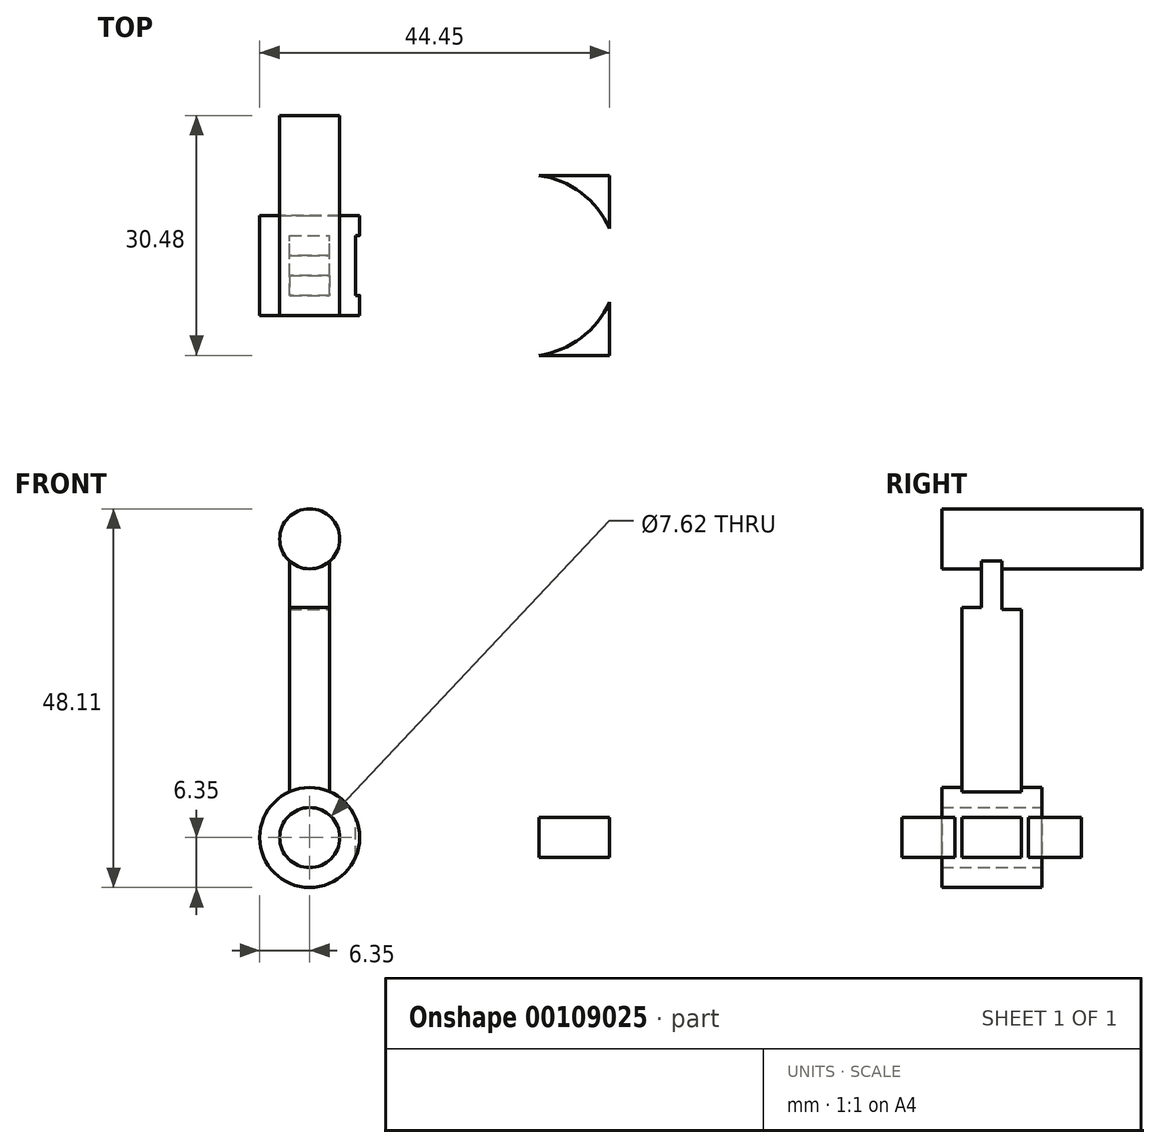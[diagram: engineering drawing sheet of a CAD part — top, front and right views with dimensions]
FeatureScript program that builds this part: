
annotation { "Feature Type Name" : "Feature", "Feature Type Description" : "" }
export const myFeature = defineFeature(function(context is Context, id is Id, definition is map)
    precondition{}
    {
        {
            var Q0;
            Q0=qCreatedBy(makeId("Front.planeOp"),FACE);
            var sketch = newSketch(context, id + "F0", { "sketchPlane" : qUnion([Q0])});
            skCircle(sketch, "E0", {"center": v(0, 0) * mm, "radius": 3.81 * mm});
            skCircle(sketch, "E1", {"center": v(0, 0) * mm, "radius": 6.35 * mm});
            skSolve(sketch);
        }
        {
            var Q0;
            Q0=makeQuery(id+"F0.imprint","IMPRINT",FACE,{"disambiguationData":[TD([[makeQuery(id+"F0.imprint","IMPRINT",EDGE,{"derivedFrom":sQuery(id+"F0.wireOp",EDGE,"E0")}),-1.0]])]});
            extrude(context, id + "F1", {"entities" : qUnion([Q0]), "depth" : 12.7 * mm});
        }
        {
            var Q0;
            Q0=qCreatedBy(makeId("Top.planeOp"),FACE);
            var sketch = newSketch(context, id + "F2", { "sketchPlane" : qUnion([Q0])});
            skLineSegment(sketch, "E2", {"start": v(0, 0) * mm, "end": v(-6.35, 0) * mm});
            skLineSegment(sketch, "E3", {"start": v(-6.35, -6.35) * mm, "end": v(-6.35, -10.16) * mm});
            skLineSegment(sketch, "E4", {"start": v(-6.35, -6.35) * mm, "end": v(-6.35, -2.54) * mm});
            skSolve(sketch);
        }
        {
            var Q0;
            Q0=qCreatedBy(makeId("Right.planeOp"),FACE);
            var sketch = newSketch(context, id + "F3", { "sketchPlane" : qUnion([Q0])});
            skLineSegment(sketch, "E5", {"start": v(-2.54, 0) * mm, "end": v(-2.54, 2.54) * mm});
            skLineSegment(sketch, "E6", {"start": v(-2.54, 0) * mm, "end": v(-2.54, -2.54) * mm});
            skLineSegment(sketch, "E7", {"start": v(-2.54, -2.54) * mm, "end": v(-10.16, -2.54) * mm});
            skLineSegment(sketch, "E8", {"start": v(-10.16, -2.54) * mm, "end": v(-10.16, 0) * mm});
            skLineSegment(sketch, "E9", {"start": v(-10.16, 0) * mm, "end": v(-10.16, 2.54) * mm});
            skLineSegment(sketch, "E10", {"start": v(-10.16, 2.54) * mm, "end": v(-2.54, 2.54) * mm});
            skSolve(sketch);
        }
        {
            var Q0;
            Q0=makeQuery(id+"F3.imprint","IMPRINT",FACE,{"disambiguationData":[TD([[makeQuery(id+"F3.imprint","IMPRINT",EDGE,{"derivedFrom":sQuery(id+"F3.wireOp",EDGE,"E5")}),1.0]])]});
            extrude(context, id + "F4", {"entities" : qUnion([Q0]), "operationType" : NewBodyOperationType.ADD, "depth" : 38.1 * mm});
        }
        {
            var Q0;
            Q0=makeQuery(id+"F0.imprint","IMPRINT",FACE,{"disambiguationData":[TD([[makeQuery(id+"F0.imprint","IMPRINT",EDGE,{"derivedFrom":sQuery(id+"F0.wireOp",EDGE,"E0")}),1.0]])]});
            extrude(context, id + "F5", {"entities" : qUnion([Q0]), "operationType" : NewBodyOperationType.REMOVE, "depth" : 25.4 * mm, "hasSecondDirection" : true, "secondDirectionOppositeDirection" : true, "secondDirectionDepth" : 25.4 * mm});
        }
        {
            var Q0;
            {var subQ1=sQuery(id+"F3.wireOp",EDGE,"E9");var subQ2=sQuery(id+"F3.wireOp",EDGE,"E8");Q0=makeQuery(id+"F4.boolean.opBoolean","SPLIT",FACE,{"disambiguationData":[TD([makeQuery(id+"F1.opExtrude","SWEPT_FACE",FACE,{"disambiguationData":[OSD([sQuery(id+"F0.wireOp",EDGE,"E1")])]})])],"derivedFrom":makeQuery(id+"F4.opExtrude","SWEPT_FACE",FACE,{"disambiguationData":[OSD([subQ2,subQ1])]})});}
            var sketch = newSketch(context, id + "F6", { "sketchPlane" : qUnion([Q0])});
            skLineSegment(sketch, "E11.bottom", {"start": v(24.28, 2.54) * mm, "end": v(38.1, 2.54) * mm});
            skLineSegment(sketch, "E11.top", {"start": v(24.28, -2.54) * mm, "end": v(38.1, -2.54) * mm});
            skLineSegment(sketch, "E11.left", {"start": v(24.28, 2.54) * mm, "end": v(24.28, -2.54) * mm});
            skLineSegment(sketch, "E11.right", {"start": v(38.1, 2.54) * mm, "end": v(38.1, -2.54) * mm});
            skSolve(sketch);
        }
        {
            var Q0;
            Q0=makeQuery(id+"F6.imprint","IMPRINT",FACE,{"disambiguationData":[TD([[makeQuery(id+"F6.imprint","IMPRINT",EDGE,{"derivedFrom":sQuery(id+"F6.wireOp",EDGE,"E11.bottom")}),1.0]])]});
            extrude(context, id + "F7", {"entities" : qUnion([Q0]), "operationType" : NewBodyOperationType.ADD, "depth" : 7.62 * mm, "hasSecondDirection" : true, "secondDirectionOppositeDirection" : true, "secondDirectionDepth" : 15.24 * mm});
        }
        {
            var Q0;
            {var subQ2=sQuery(id+"F6.wireOp",EDGE,"E11.left");Q0=makeQuery(id+"F7.boolean.opBoolean","SPLIT",FACE,{"disambiguationData":[TD([makeQuery(id+"F4.opExtrude","SWEPT_FACE",FACE,{"disambiguationData":[OSD([sQuery(id+"F3.wireOp",EDGE,"E8"),sQuery(id+"F3.wireOp",EDGE,"E9")])]})])],"derivedFrom":makeQuery(id+"F7.opExtrude","SWEPT_FACE",FACE,{"disambiguationData":[OSD([subQ2])]})});}
            extrude(context, id + "F8", {"entities" : qUnion([Q0]), "operationType" : NewBodyOperationType.ADD, "depth" : 7.62 * mm});
        }
        {
            var Q0;
            {var subQ1=sQuery(id+"F6.wireOp",EDGE,"E11.left");Q0=makeQuery(id+"F7.boolean.opBoolean","SPLIT",FACE,{"disambiguationData":[TD([makeQuery(id+"F4.opExtrude","SWEPT_FACE",FACE,{"disambiguationData":[OSD([sQuery(id+"F3.wireOp",EDGE,"E5"),sQuery(id+"F3.wireOp",EDGE,"E6")])]})])],"derivedFrom":makeQuery(id+"F7.opExtrude","SWEPT_FACE",FACE,{"disambiguationData":[OSD([subQ1])]})});}
            extrude(context, id + "F9", {"entities" : qUnion([Q0]), "operationType" : NewBodyOperationType.ADD, "depth" : 7.62 * mm});
        }
        {
            var Q0;
            {var subQ0=sQuery(id+"F6.wireOp",EDGE,"E11.left");var subQ1=sQuery(id+"F6.wireOp",EDGE,"E11.bottom");var subQ2=sQuery(id+"F3.wireOp",EDGE,"E10");var subQ3=sQuery(id+"F3.wireOp",EDGE,"E9");Q0=makeQuery(id+"F9.boolean.opBoolean","MERGE",FACE,{"derivedFrom":[makeQuery(id+"F8.boolean.opBoolean","MERGE",FACE,{"derivedFrom":[makeQuery(id+"F7.boolean.opBoolean","MERGE",FACE,{"derivedFrom":[makeQuery(id+"F4.boolean.opBoolean","SPLIT",FACE,{"disambiguationData":[TD([makeQuery(id+"F1.opExtrude","SWEPT_FACE",FACE,{"disambiguationData":[OSD([sQuery(id+"F0.wireOp",EDGE,"E1")])]})])],"derivedFrom":makeQuery(id+"F4.opExtrude","SWEPT_FACE",FACE,{"disambiguationData":[OSD([subQ2])]})}),makeQuery(id+"F7.opExtrude","SWEPT_FACE",FACE,{"disambiguationData":[OSD([subQ1])]})]}),makeQuery(id+"F8.opExtrude","SWEPT_FACE",FACE,{"disambiguationData":[OSD([subQ3,subQ2,subQ1,subQ0])]})]}),makeQuery(id+"F9.opExtrude","SWEPT_FACE",FACE,{"disambiguationData":[OSD([subQ3,subQ2,subQ1,subQ0])]})]});}
            var sketch = newSketch(context, id + "F10", { "sketchPlane" : qUnion([Q0])});
            skArc(sketch, "E12", {"start": v(16.66, -2.54) * mm, "mid": v(39.08, -6.35) * mm, "end": v(16.66, -10.16) * mm});
            skLineSegment(sketch, "E13", {"start": v(16.66, -2.54) * mm, "end": v(16.66, 5.08) * mm});
            skLineSegment(sketch, "E14", {"start": v(16.66, 5.08) * mm, "end": v(38.1, 5.08) * mm});
            skLineSegment(sketch, "E15", {"start": v(38.1, 5.08) * mm, "end": v(38.1, -17.78) * mm});
            skLineSegment(sketch, "E16", {"start": v(38.1, -17.78) * mm, "end": v(16.66, -17.78) * mm});
            skLineSegment(sketch, "E17", {"start": v(16.66, -17.78) * mm, "end": v(16.66, -10.16) * mm});
            skSolve(sketch);
        }
        {
            var Q0;
            {var subQ0=sQuery(id+"F10.wireOp",EDGE,"E17");Q0=makeQuery(id+"F10.imprint","IMPRINT",FACE,{"disambiguationData":[TD([[makeQuery(id+"F10.imprint","IMPRINT",EDGE,{"derivedFrom":subQ0}),-1.0]])]});}
            var Q1;
            {var subQ0=sQuery(id+"F10.wireOp",EDGE,"E13");Q1=makeQuery(id+"F10.imprint","IMPRINT",FACE,{"disambiguationData":[TD([[makeQuery(id+"F10.imprint","IMPRINT",EDGE,{"derivedFrom":subQ0}),-1.0]])]});}
            var Q2;
            {var subQ0=sQuery(id+"F10.wireOp",EDGE,"E14");var subQ1=sQuery(id+"F10.wireOp",EDGE,"E12");var subQ2=makeQuery(id+"F10.imprint","INTERSECT",VERTEX,{"disambiguationData":[OD(1.0)],"derivedFrom":[subQ1,subQ0]});Q2=makeQuery(id+"F10.imprint","IMPRINT",FACE,{"disambiguationData":[TD([[makeQuery(id+"F10.imprint","IMPRINT",EDGE,{"disambiguationData":[TD([[subQ2,-1.0]])],"derivedFrom":subQ1}),1.0]])]});}
            var Q3;
            {var subQ0=sQuery(id+"F10.wireOp",EDGE,"E15");var subQ1=sQuery(id+"F10.wireOp",EDGE,"E12");var subQ2=makeQuery(id+"F10.imprint","INTERSECT",VERTEX,{"disambiguationData":[OD(1.0)],"derivedFrom":[subQ1,subQ0]});Q3=makeQuery(id+"F10.imprint","IMPRINT",FACE,{"disambiguationData":[TD([[makeQuery(id+"F10.imprint","IMPRINT",EDGE,{"disambiguationData":[TD([[subQ2,-1.0]])],"derivedFrom":subQ1}),1.0]])]});}
            extrude(context, id + "F11", {"entities" : qUnion([Q0, Q1, Q2, Q3]), "operationType" : NewBodyOperationType.REMOVE, "oppositeDirection" : true, "depth" : 25.4 * mm});
        }
        {
            var Q0;
            {var subQ0=sQuery(id+"F10.wireOp",EDGE,"E15");var subQ1=sQuery(id+"F10.wireOp",EDGE,"E12");var subQ2=makeQuery(id+"F10.imprint","INTERSECT",VERTEX,{"disambiguationData":[OD(0.0)],"derivedFrom":[subQ1,subQ0]});Q0=makeQuery(id+"F10.imprint","IMPRINT",FACE,{"disambiguationData":[TD([[makeQuery(id+"F10.imprint","IMPRINT",EDGE,{"disambiguationData":[TD([[subQ2,-1.0]])],"derivedFrom":subQ1}),-1.0]])]});}
            extrude(context, id + "F12", {"entities" : qUnion([Q0]), "operationType" : NewBodyOperationType.ADD, "oppositeDirection" : true, "depth" : 5.08 * mm});
        }
        {
            var Q0;
            Q0=qCreatedBy(makeId("Top.planeOp"),FACE);
            var sketch = newSketch(context, id + "F13", { "sketchPlane" : qUnion([Q0])});
            skLineSegment(sketch, "E18", {"start": v(0, -2.54) * mm, "end": v(-2.54, -2.54) * mm});
            skLineSegment(sketch, "E19", {"start": v(0, -2.54) * mm, "end": v(2.54, -2.54) * mm});
            skLineSegment(sketch, "E20", {"start": v(2.54, -2.54) * mm, "end": v(2.54, -10.16) * mm});
            skLineSegment(sketch, "E21", {"start": v(-2.54, -2.54) * mm, "end": v(-2.54, -10.16) * mm});
            skLineSegment(sketch, "E22", {"start": v(-2.54, -10.16) * mm, "end": v(0, -10.16) * mm});
            skLineSegment(sketch, "E23", {"start": v(0, -10.16) * mm, "end": v(2.54, -10.16) * mm});
            skSolve(sketch);
        }
        {
            var Q0;
            Q0=makeQuery(id+"F13.imprint","IMPRINT",FACE,{"disambiguationData":[TD([[makeQuery(id+"F13.imprint","IMPRINT",EDGE,{"derivedFrom":sQuery(id+"F13.wireOp",EDGE,"E18")}),1.0]])]});
            extrude(context, id + "F14", {"entities" : qUnion([Q0]), "operationType" : NewBodyOperationType.ADD, "depth" : 38.1 * mm});
        }
        {
            var Q0;
            Q0=makeQuery(id+"F0.imprint","IMPRINT",FACE,{"disambiguationData":[TD([[makeQuery(id+"F0.imprint","IMPRINT",EDGE,{"derivedFrom":sQuery(id+"F0.wireOp",EDGE,"E0")}),1.0]])]});
            extrude(context, id + "F15", {"entities" : qUnion([Q0]), "operationType" : NewBodyOperationType.REMOVE, "depth" : 25.4 * mm});
        }
        {
            var Q0;
            {var subQ2=sQuery(id+"F13.wireOp",EDGE,"E19");var subQ3=sQuery(id+"F13.wireOp",EDGE,"E18");Q0=makeQuery(id+"F14.boolean.opBoolean","SPLIT",FACE,{"disambiguationData":[TD([makeQuery(id+"F1.opExtrude","SWEPT_FACE",FACE,{"disambiguationData":[OSD([sQuery(id+"F0.wireOp",EDGE,"E1")])]})])],"derivedFrom":makeQuery(id+"F14.opExtrude","SWEPT_FACE",FACE,{"disambiguationData":[OSD([subQ3,subQ2])]})});}
            var sketch = newSketch(context, id + "F16", { "sketchPlane" : qUnion([Q0])});
            skLineSegment(sketch, "E24", {"start": v(0, 38.1) * mm, "end": v(0, 28.96) * mm});
            skPoint(sketch, "E24.endSnap0", {"position": v(0, 38.1) * mm});
            skLineSegment(sketch, "E25", {"start": v(0, 28.96) * mm, "end": v(-2.54, 28.96) * mm});
            skLineSegment(sketch, "E26", {"start": v(-2.54, 28.96) * mm, "end": v(-2.54, 38.1) * mm});
            skLineSegment(sketch, "E27", {"start": v(-2.54, 38.1) * mm, "end": v(0, 38.1) * mm});
            skLineSegment(sketch, "E28", {"start": v(0, 38.1) * mm, "end": v(2.54, 38.1) * mm});
            skLineSegment(sketch, "E29", {"start": v(2.54, 38.1) * mm, "end": v(2.54, 28.96) * mm});
            skLineSegment(sketch, "E30", {"start": v(0, 28.96) * mm, "end": v(2.54, 28.96) * mm});
            skSolve(sketch);
        }
        {
            var Q0;
            Q0=makeQuery(id+"F16.imprint","IMPRINT",FACE,{"disambiguationData":[TD([[makeQuery(id+"F16.imprint","IMPRINT",EDGE,{"derivedFrom":sQuery(id+"F16.wireOp",EDGE,"E24")}),-1.0]])]});
            var Q1;
            Q1=makeQuery(id+"F16.imprint","IMPRINT",FACE,{"disambiguationData":[TD([[makeQuery(id+"F16.imprint","IMPRINT",EDGE,{"derivedFrom":sQuery(id+"F16.wireOp",EDGE,"E24")}),1.0]])]});
            extrude(context, id + "F17", {"entities" : qUnion([Q0, Q1]), "operationType" : NewBodyOperationType.REMOVE, "oppositeDirection" : true, "depth" : 2.54 * mm});
        }
        {
            var Q0;
            {var subQ0=sQuery(id+"F13.wireOp",EDGE,"E23");var subQ1=sQuery(id+"F13.wireOp",EDGE,"E22");Q0=makeQuery(id+"F14.boolean.opBoolean","SPLIT",FACE,{"disambiguationData":[TD([makeQuery(id+"F1.opExtrude","SWEPT_FACE",FACE,{"disambiguationData":[OSD([sQuery(id+"F0.wireOp",EDGE,"E1")])]})])],"derivedFrom":makeQuery(id+"F14.opExtrude","SWEPT_FACE",FACE,{"disambiguationData":[OSD([subQ1,subQ0])]})});}
            var sketch = newSketch(context, id + "F18", { "sketchPlane" : qUnion([Q0])});
            skLineSegment(sketch, "E31", {"start": v(0, 38.1) * mm, "end": v(0, 29.21) * mm});
            skPoint(sketch, "E31.endSnap0", {"position": v(0, 38.1) * mm});
            skLineSegment(sketch, "E32", {"start": v(0, 29.21) * mm, "end": v(2.54, 29.21) * mm});
            skLineSegment(sketch, "E33", {"start": v(0, 29.21) * mm, "end": v(-2.54, 29.21) * mm});
            skSolve(sketch);
        }
        {
            var Q0;
            {var subQ0=sQuery(id+"F18.wireOp",EDGE,"E31");Q0=makeQuery(id+"F18.imprint","IMPRINT",FACE,{"disambiguationData":[TD([[makeQuery(id+"F18.imprint","IMPRINT",EDGE,{"derivedFrom":subQ0}),-1.0]])]});}
            var Q1;
            {var subQ0=sQuery(id+"F18.wireOp",EDGE,"E31");Q1=makeQuery(id+"F18.imprint","IMPRINT",FACE,{"disambiguationData":[TD([[makeQuery(id+"F18.imprint","IMPRINT",EDGE,{"derivedFrom":subQ0}),1.0]])]});}
            extrude(context, id + "F19", {"entities" : qUnion([Q0, Q1]), "operationType" : NewBodyOperationType.REMOVE, "oppositeDirection" : true, "depth" : 2.54 * mm});
        }
        {
            var Q0;
            Q0=qCreatedBy(makeId("Front.planeOp"),FACE);
            var sketch = newSketch(context, id + "F20", { "sketchPlane" : qUnion([Q0])});
            skCircle(sketch, "E34", {"center": v(0, 37.95) * mm, "radius": 3.81 * mm});
            skLineSegment(sketch, "E35", {"start": v(0, 37.95) * mm, "end": v(0, 0) * mm});
            skSolve(sketch);
        }
        {
            var Q0;
            Q0=makeQuery(id+"F20.imprint","IMPRINT",FACE,{"disambiguationData":[TD([[makeQuery(id+"F20.imprint","IMPRINT",EDGE,{"derivedFrom":sQuery(id+"F20.wireOp",EDGE,"E34")}),1.0]])]});
            extrude(context, id + "F21", {"entities" : qUnion([Q0]), "operationType" : NewBodyOperationType.ADD, "depth" : 12.7 * mm, "hasSecondDirection" : true, "secondDirectionOppositeDirection" : true, "secondDirectionDepth" : 12.7 * mm});
        }
    });
